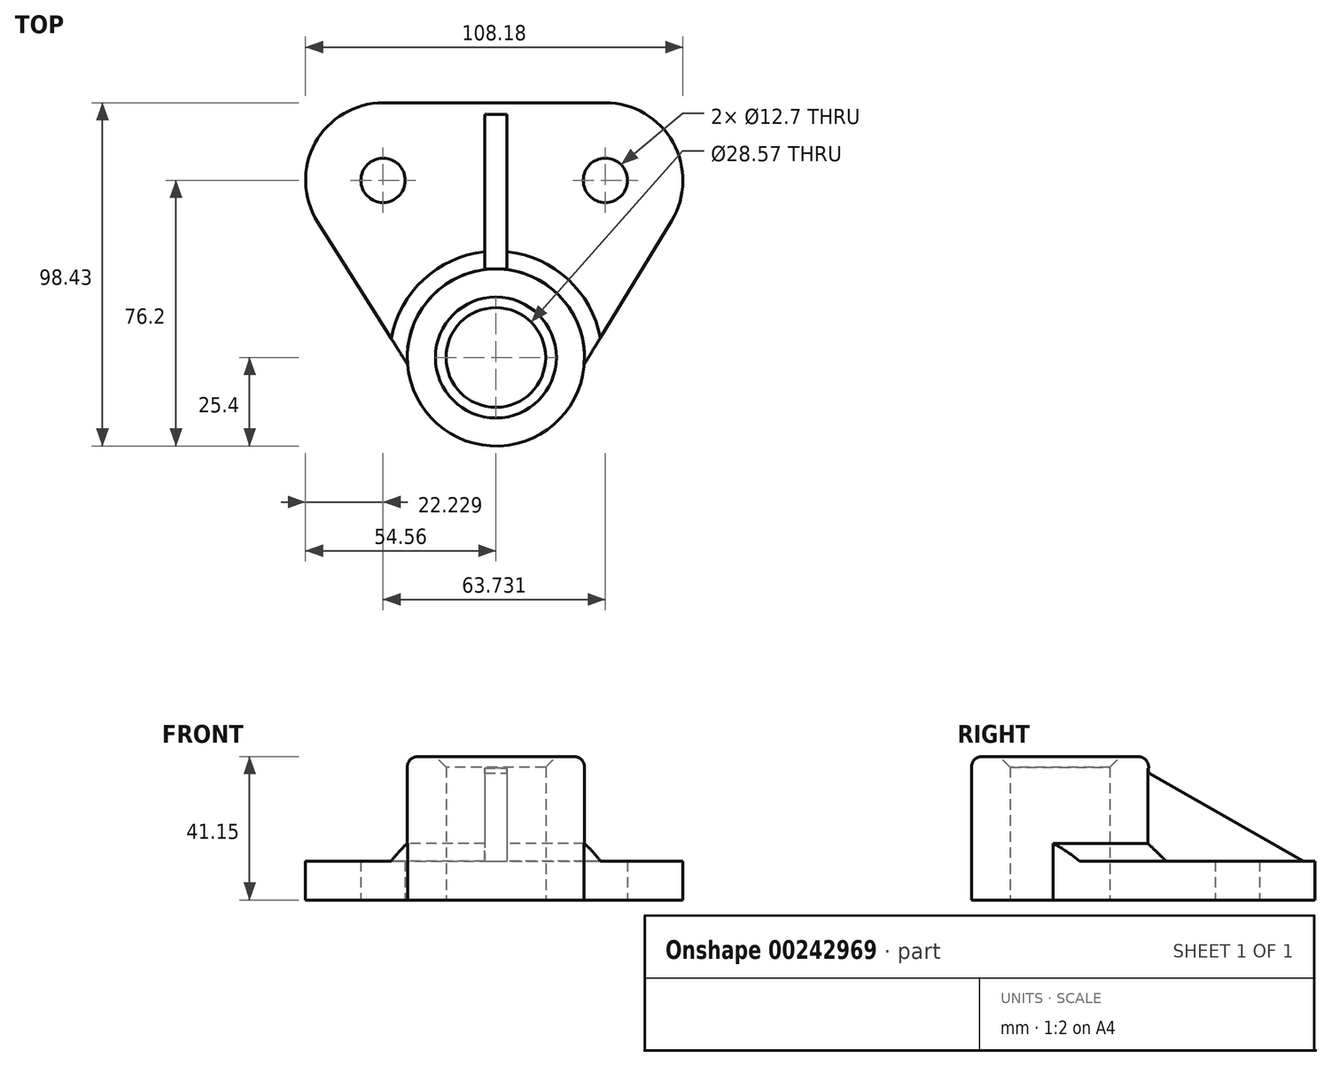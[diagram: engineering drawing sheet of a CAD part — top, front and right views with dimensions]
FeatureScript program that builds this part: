
annotation { "Feature Type Name" : "Feature", "Feature Type Description" : "" }
export const myFeature = defineFeature(function(context is Context, id is Id, definition is map)
    precondition{}
    {
        {
            var Q0;
            Q0=qCreatedBy(makeId("Top.planeOp"),FACE);
            var sketch = newSketch(context, id + "F0", { "sketchPlane" : qUnion([Q0])});
            skCircle(sketch, "E0", {"center": v(0, 0) * mm, "radius": 25.4 * mm});
            skCircle(sketch, "E1", {"center": v(-32.33, 50.8) * mm, "radius": 22.23 * mm});
            skCircle(sketch, "E2", {"center": v(31.4, 50.8) * mm, "radius": 22.23 * mm});
            skLineSegment(sketch, "E3", {"start": v(-32.33, 73.03) * mm, "end": v(31.4, 73.03) * mm});
            skCircle(sketch, "E4", {"center": v(0, 0) * mm, "radius": 14.31 * mm});
            skCircle(sketch, "E5", {"center": v(-32.33, 50.8) * mm, "radius": 6.35 * mm});
            skCircle(sketch, "E6", {"center": v(31.4, 50.8) * mm, "radius": 6.35 * mm});
            skLineSegment(sketch, "E7", {"start": v(-25.32, -2) * mm, "end": v(-51.13, 38.95) * mm});
            skLineSegment(sketch, "E8", {"start": v(25.32, -2) * mm, "end": v(50.4, 39.26) * mm});
            skSolve(sketch);
        }
        {
            var Q0;
            Q0=qSketchRegion(id+"F0",true);
            extrude(context, id + "F1", {"entities" : qUnion([Q0]), "depth" : 11.18 * mm});
        }
        {
            var Q0;
            Q0=qCreatedBy(makeId("Top.planeOp"),FACE);
            var sketch = newSketch(context, id + "F2", { "sketchPlane" : qUnion([Q0])});
            skCircle(sketch, "E9", {"center": v(0, 0) * mm, "radius": 25.4 * mm});
            skCircle(sketch, "E10", {"center": v(0, 0) * mm, "radius": 14.29 * mm});
            skSolve(sketch);
        }
        {
            var Q0;
            Q0=qSketchRegion(id+"F2",true);
            extrude(context, id + "F3", {"entities" : qUnion([Q0]), "operationType" : NewBodyOperationType.ADD, "depth" : 41.15 * mm});
        }
        {
            var Q0;
            Q0=makeQuery(id+"F3.opExtrude","CAP_EDGE",EDGE,{"disambiguationData":[OSD([sQuery(id+"F2.wireOp",EDGE,"E9")])],"isStart":false});
            fillet(context, id + "F4", {"entities" : qUnion([Q0]), "radius" : 3.05 * mm, "tangentPropagation" : true, "allowEdgeOverflow" : false});
        }
        {
            var Q0;
            Q0=makeQuery(id+"F1.opExtrude","CAP_FACE",FACE,{"disambiguationData":[OSD([sQuery(id+"F0.wireOp",EDGE,"E0"),sQuery(id+"F0.wireOp",EDGE,"E1"),sQuery(id+"F0.wireOp",EDGE,"E2"),sQuery(id+"F0.wireOp",EDGE,"E3"),sQuery(id+"F0.wireOp",EDGE,"E4"),sQuery(id+"F0.wireOp",EDGE,"E5"),sQuery(id+"F0.wireOp",EDGE,"E6"),sQuery(id+"F0.wireOp",EDGE,"E7"),sQuery(id+"F0.wireOp",EDGE,"E8")])],"isStart":false});
            var sketch = newSketch(context, id + "F5", { "sketchPlane" : qUnion([Q0])});
            skLineSegment(sketch, "E11", {"start": v(0, 73.03) * mm, "end": v(0, 69.72) * mm});
            skLineSegment(sketch, "E12", {"start": v(0, 69.72) * mm, "end": v(3.18, 69.72) * mm});
            skLineSegment(sketch, "E13", {"start": v(3.18, 69.72) * mm, "end": v(3.18, 25.2) * mm});
            skLineSegment(sketch, "E14", {"start": v(0, 69.72) * mm, "end": v(-3.17, 69.72) * mm});
            skLineSegment(sketch, "E15", {"start": v(-3.17, 69.72) * mm, "end": v(-3.17, 25.2) * mm});
            skSolve(sketch);
        }
        {
            var Q0;
            Q0=makeQuery(id+"F5.imprint","IMPRINT",FACE,{"disambiguationData":[TD([[makeQuery(id+"F5.imprint","IMPRINT",EDGE,{"derivedFrom":sQuery(id+"F5.wireOp",EDGE,"E12")}),-1.0]])]});
            extrude(context, id + "F6", {"entities" : qUnion([Q0]), "operationType" : NewBodyOperationType.ADD, "depth" : 26.67 * mm});
        }
        {
            var Q0;
            Q0=makeQuery(id+"F6.opExtrude","SWEPT_FACE",FACE,{"disambiguationData":[OSD([sQuery(id+"F5.wireOp",EDGE,"E13")])]});
            var sketch = newSketch(context, id + "F7", { "sketchPlane" : qUnion([Q0])});
            skLineSegment(sketch, "E16", {"start": v(25.4, 36.37) * mm, "end": v(69.72, 11.18) * mm});
            skLineSegment(sketch, "E17", {"start": v(69.72, 11.18) * mm, "end": v(69.72, 37.85) * mm});
            skLineSegment(sketch, "E18", {"start": v(25.4, 36.37) * mm, "end": v(25.2, 37.85) * mm});
            skLineSegment(sketch, "E19", {"start": v(25.2, 37.85) * mm, "end": v(69.72, 37.85) * mm});
            skSolve(sketch);
        }
        {
            var Q0;
            Q0=makeQuery(id+"F7.imprint","IMPRINT",FACE,{"disambiguationData":[TD([[makeQuery(id+"F7.imprint","IMPRINT",EDGE,{"derivedFrom":sQuery(id+"F7.wireOp",EDGE,"E16")}),1.0]])]});
            extrude(context, id + "F8", {"entities" : qUnion([Q0]), "operationType" : NewBodyOperationType.REMOVE, "oppositeDirection" : true, "depth" : 36.58 * mm});
        }
        {
            var Q0;
            Q0=makeQuery(id+"F3.opExtrude","CAP_EDGE",EDGE,{"disambiguationData":[OSD([sQuery(id+"F2.wireOp",EDGE,"E10")])],"isStart":false});
            chamfer(context, id + "F9", {"entities" : qUnion([Q0]), "width" : 3.05 * mm, "tangentPropagation" : true});
        }
        {
            var Q0;
            {var subQ0=sQuery(id+"F0.wireOp",EDGE,"E7");var subQ1=sQuery(id+"F0.wireOp",EDGE,"E0");var subQ2=makeQuery(id+"F1.opExtrude","CAP_FACE",FACE,{"disambiguationData":[OSD([subQ1,sQuery(id+"F0.wireOp",EDGE,"E1"),sQuery(id+"F0.wireOp",EDGE,"E2"),sQuery(id+"F0.wireOp",EDGE,"E3"),sQuery(id+"F0.wireOp",EDGE,"E4"),sQuery(id+"F0.wireOp",EDGE,"E5"),sQuery(id+"F0.wireOp",EDGE,"E6"),subQ0,sQuery(id+"F0.wireOp",EDGE,"E8")])],"isStart":false});var subQ3=makeQuery(id+"F3.opExtrude","SWEPT_FACE",FACE,{"disambiguationData":[OSD([sQuery(id+"F2.wireOp",EDGE,"E9")])]});Q0=makeQuery(id+"F6.boolean.opBoolean","SPLIT",EDGE,{"disambiguationData":[TD([makeQuery(id+"F1.opExtrude","SWEPT_FACE",FACE,{"disambiguationData":[OSD([subQ0])]})])],"derivedFrom":makeQuery(id+"F3.boolean.opBoolean","INTERSECT",EDGE,{"derivedFrom":[subQ2,subQ3]})});}
            var Q1;
            {var subQ0=sQuery(id+"F0.wireOp",EDGE,"E8");var subQ1=sQuery(id+"F0.wireOp",EDGE,"E0");var subQ2=makeQuery(id+"F1.opExtrude","CAP_FACE",FACE,{"disambiguationData":[OSD([subQ1,sQuery(id+"F0.wireOp",EDGE,"E1"),sQuery(id+"F0.wireOp",EDGE,"E2"),sQuery(id+"F0.wireOp",EDGE,"E3"),sQuery(id+"F0.wireOp",EDGE,"E4"),sQuery(id+"F0.wireOp",EDGE,"E5"),sQuery(id+"F0.wireOp",EDGE,"E6"),sQuery(id+"F0.wireOp",EDGE,"E7"),subQ0])],"isStart":false});var subQ3=makeQuery(id+"F3.opExtrude","SWEPT_FACE",FACE,{"disambiguationData":[OSD([sQuery(id+"F2.wireOp",EDGE,"E9")])]});Q1=makeQuery(id+"F6.boolean.opBoolean","SPLIT",EDGE,{"disambiguationData":[TD([makeQuery(id+"F1.opExtrude","SWEPT_FACE",FACE,{"disambiguationData":[OSD([subQ0])]})])],"derivedFrom":makeQuery(id+"F3.boolean.opBoolean","INTERSECT",EDGE,{"derivedFrom":[subQ2,subQ3]})});}
            chamfer(context, id + "F10", {"entities" : qUnion([Q0, Q1]), "width" : 5.08 * mm, "tangentPropagation" : true});
        }
    });
